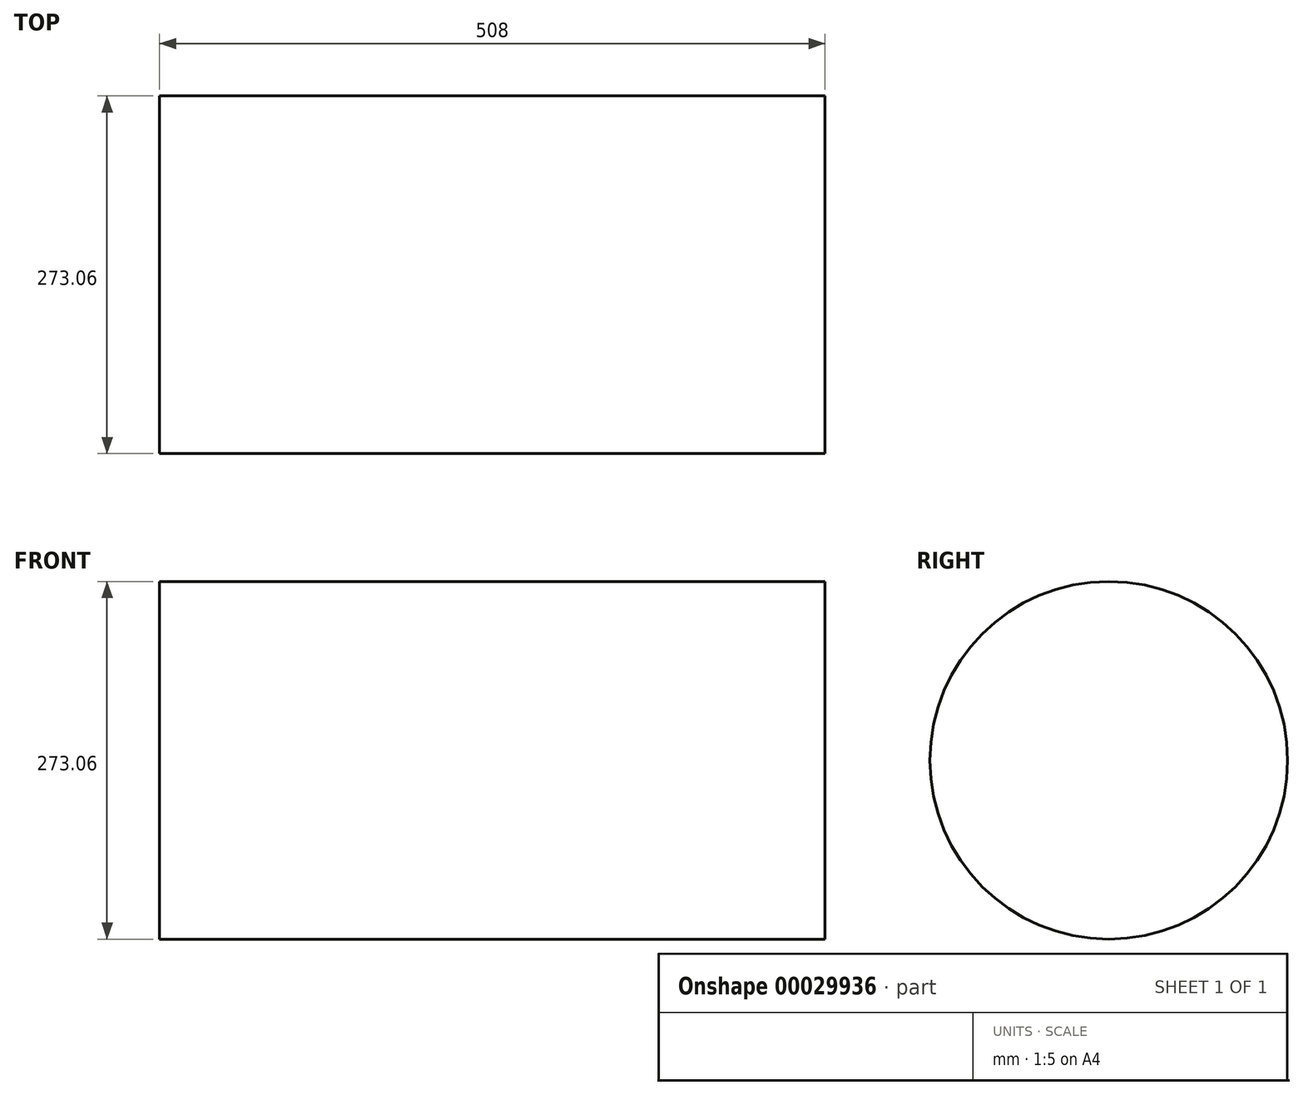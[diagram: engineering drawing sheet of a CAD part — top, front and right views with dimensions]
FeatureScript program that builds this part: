
annotation { "Feature Type Name" : "Feature", "Feature Type Description" : "" }
export const myFeature = defineFeature(function(context is Context, id is Id, definition is map)
    precondition{}
    {
        {
            var Q0;
            Q0=qCreatedBy(makeId("Right.planeOp"),FACE);
            var sketch = newSketch(context, id + "F0", { "sketchPlane" : qUnion([Q0])});
            skCircle(sketch, "E0", {"center": v(0, 0) * mm, "radius": 136.53 * mm});
            skSolve(sketch);
        }
        {
            var Q0;
            Q0=makeQuery(id+"F0.imprint","IMPRINT",FACE,{"disambiguationData":[TD([[makeQuery(id+"F0.imprint","IMPRINT",EDGE,{"derivedFrom":sQuery(id+"F0.wireOp",EDGE,"E0")}),1.0]])]});
            extrude(context, id + "F1", {"entities" : qUnion([Q0]), "depth" : 508 * mm});
        }
    });
